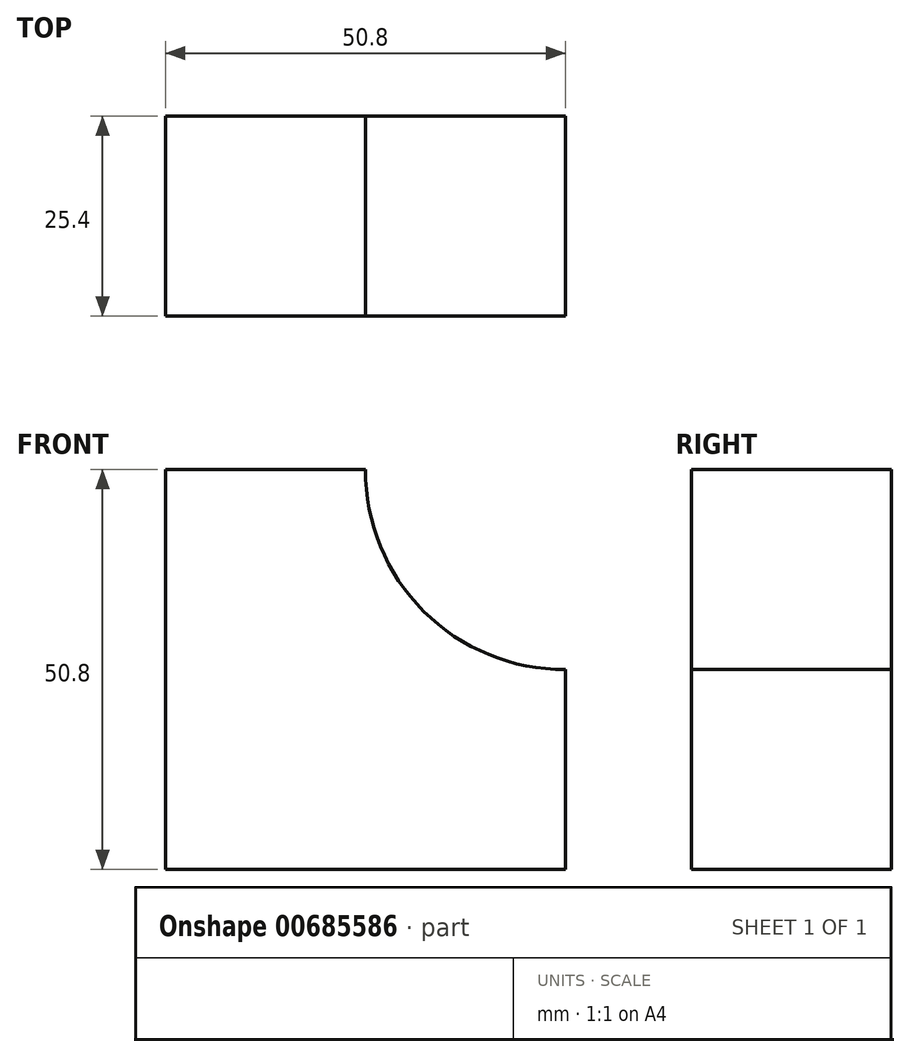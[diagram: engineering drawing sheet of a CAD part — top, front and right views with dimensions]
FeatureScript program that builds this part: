
annotation { "Feature Type Name" : "Feature", "Feature Type Description" : "" }
export const myFeature = defineFeature(function(context is Context, id is Id, definition is map)
    precondition{}
    {
        {
            var Q0;
            Q0=qCreatedBy(makeId("Front.planeOp"),FACE);
            var sketch = newSketch(context, id + "F0", { "sketchPlane" : qUnion([Q0])});
            skLineSegment(sketch, "E0", {"start": v(0, 0) * mm, "end": v(-50.8, 0) * mm});
            skLineSegment(sketch, "E1", {"start": v(-50.8, 0) * mm, "end": v(-50.8, 50.8) * mm});
            skLineSegment(sketch, "E2", {"start": v(-50.8, 50.8) * mm, "end": v(-25.4, 50.8) * mm});
            skLineSegment(sketch, "E3", {"start": v(0, 0) * mm, "end": v(0, 25.4) * mm});
            skArc(sketch, "E4", {"start": v(-25.4, 50.8) * mm, "mid": v(-18.01, 32.79) * mm, "end": v(0, 25.4) * mm});
            skSolve(sketch);
        }
        {
            var Q0;
            Q0 = qSketchRegion(id + "F0", true);
            extrude(context, id + "F1", {"entities" : qUnion([Q0]), "depth" : 25.4 * mm, "offsetDistance" : 25.4 * mm});
        }
    });
